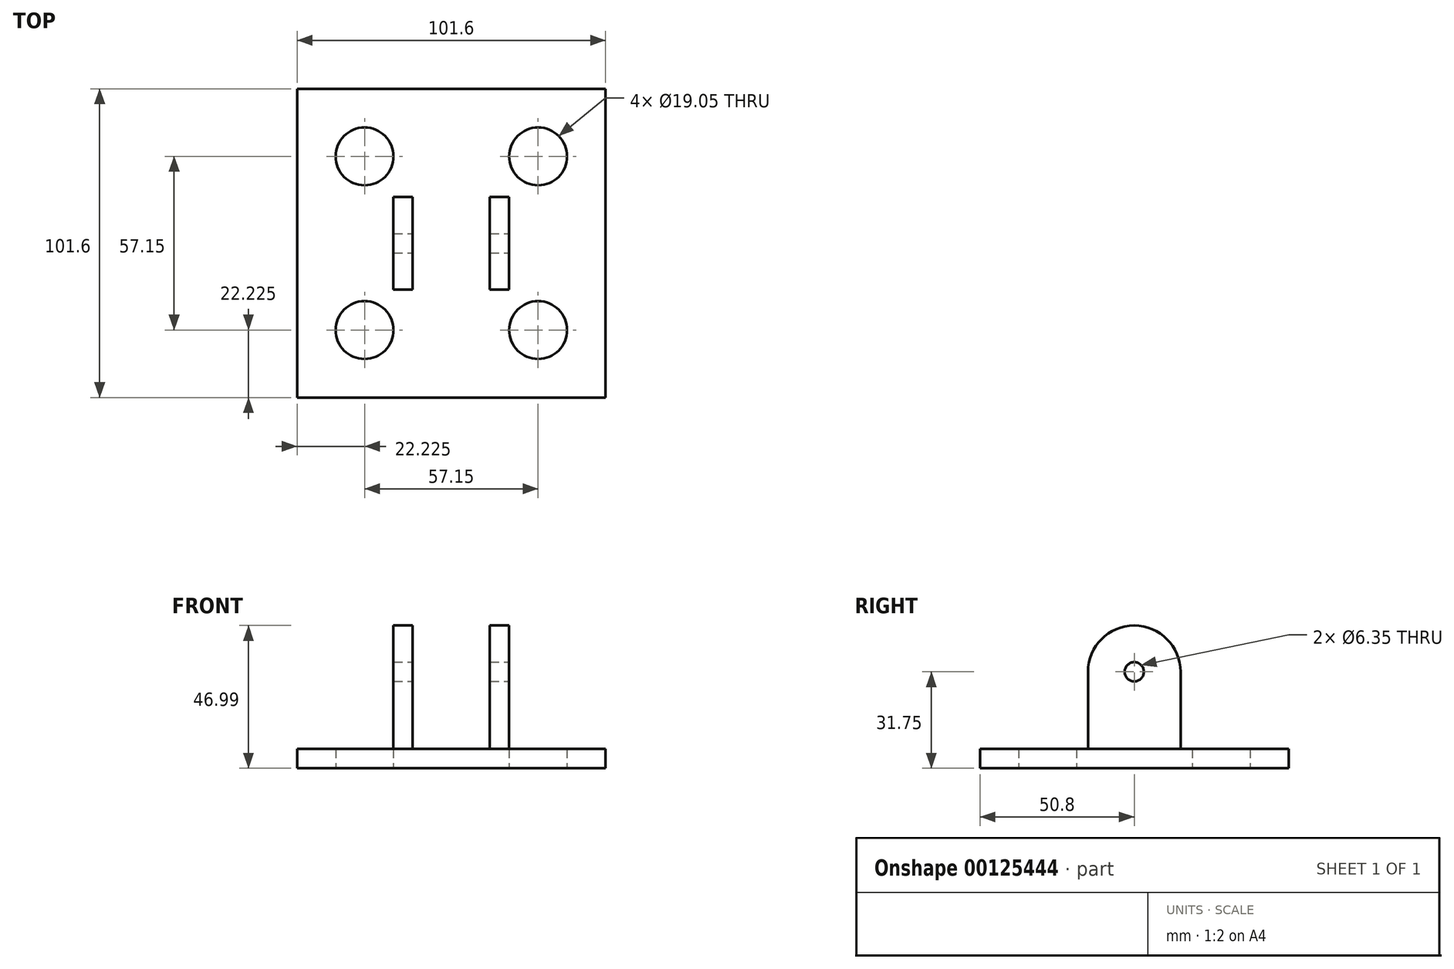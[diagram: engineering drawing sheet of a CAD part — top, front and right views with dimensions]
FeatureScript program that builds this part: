
annotation { "Feature Type Name" : "Feature", "Feature Type Description" : "" }
export const myFeature = defineFeature(function(context is Context, id is Id, definition is map)
    precondition{}
    {
        {
            var Q0;
            Q0=qCreatedBy(makeId("Top.planeOp"),FACE);
            var sketch = newSketch(context, id + "F0", { "sketchPlane" : qUnion([Q0])});
            skLineSegment(sketch, "E0.bottom", {"start": v(50.8, -50.8) * mm, "end": v(-50.8, -50.8) * mm});
            skLineSegment(sketch, "E0.top", {"start": v(50.8, 50.8) * mm, "end": v(-50.8, 50.8) * mm});
            skLineSegment(sketch, "E0.left", {"start": v(50.8, -50.8) * mm, "end": v(50.8, 50.8) * mm});
            skLineSegment(sketch, "E0.right", {"start": v(-50.8, -50.8) * mm, "end": v(-50.8, 50.8) * mm});
            skPoint(sketch, "E0.middle", {"position": v(0, 0) * mm});
            skCircle(sketch, "E1", {"center": v(-28.58, 28.58) * mm, "radius": 9.53 * mm});
            skCircle(sketch, "E2.MirrorC", {"center": v(28.58, 28.58) * mm, "radius": 9.53 * mm});
            skCircle(sketch, "E3.MirrorC", {"center": v(28.58, -28.58) * mm, "radius": 9.53 * mm});
            skCircle(sketch, "E4.MirrorC", {"center": v(-28.58, -28.58) * mm, "radius": 9.53 * mm});
            skSolve(sketch);
        }
        {
            var Q0;
            Q0=makeQuery(id+"F0.imprint","IMPRINT",FACE,{"disambiguationData":[TD([[makeQuery(id+"F0.imprint","IMPRINT",EDGE,{"derivedFrom":sQuery(id+"F0.wireOp",EDGE,"E0.bottom")}),-1.0]])]});
            extrude(context, id + "F1", {"entities" : qUnion([Q0]), "depth" : 6.35 * mm});
        }
        {
            var Q0;
            Q0=makeQuery(id+"F1.opExtrude","CAP_FACE",FACE,{"disambiguationData":[OSD([sQuery(id+"F0.wireOp",EDGE,"E0.bottom"),sQuery(id+"F0.wireOp",EDGE,"E0.top"),sQuery(id+"F0.wireOp",EDGE,"E0.left"),sQuery(id+"F0.wireOp",EDGE,"E0.right"),sQuery(id+"F0.wireOp",EDGE,"E1"),sQuery(id+"F0.wireOp",EDGE,"E2.MirrorC"),sQuery(id+"F0.wireOp",EDGE,"E3.MirrorC"),sQuery(id+"F0.wireOp",EDGE,"E4.MirrorC")])],"isStart":false});
            var sketch = newSketch(context, id + "F2", { "sketchPlane" : qUnion([Q0])});
            skLineSegment(sketch, "E5.bottom", {"start": v(12.7, -15.24) * mm, "end": v(-12.7, -15.24) * mm});
            skLineSegment(sketch, "E5.top", {"start": v(12.7, 15.24) * mm, "end": v(-12.7, 15.24) * mm});
            skLineSegment(sketch, "E5.left", {"start": v(12.7, -15.24) * mm, "end": v(12.7, 15.24) * mm});
            skLineSegment(sketch, "E5.right", {"start": v(-12.7, -15.24) * mm, "end": v(-12.7, 15.24) * mm});
            skPoint(sketch, "E5.middle", {"position": v(0, 0) * mm});
            skLineSegment(sketch, "E6.bottom", {"start": v(19.05, -15.24) * mm, "end": v(-19.05, -15.24) * mm});
            skLineSegment(sketch, "E6.top", {"start": v(19.05, 15.24) * mm, "end": v(-19.05, 15.24) * mm});
            skLineSegment(sketch, "E6.left", {"start": v(19.05, -15.24) * mm, "end": v(19.05, 15.24) * mm});
            skLineSegment(sketch, "E6.right", {"start": v(-19.05, -15.24) * mm, "end": v(-19.05, 15.24) * mm});
            skSolve(sketch);
        }
        {
            var Q0;
            {var subQ0=sQuery(id+"F2.wireOp",EDGE,"E5.left");Q0=makeQuery(id+"F2.imprint","IMPRINT",FACE,{"disambiguationData":[TD([[makeQuery(id+"F2.imprint","IMPRINT",EDGE,{"derivedFrom":subQ0}),-1.0]])]});}
            var Q1;
            {var subQ0=sQuery(id+"F2.wireOp",EDGE,"E5.right");Q1=makeQuery(id+"F2.imprint","IMPRINT",FACE,{"disambiguationData":[TD([[makeQuery(id+"F2.imprint","IMPRINT",EDGE,{"derivedFrom":subQ0}),1.0]])]});}
            extrude(context, id + "F3", {"entities" : qUnion([Q0, Q1]), "operationType" : NewBodyOperationType.ADD, "depth" : 25.4 * mm});
        }
        {
            var Q0;
            Q0=makeQuery(id+"F3.opExtrude","CAP_FACE",FACE,{"disambiguationData":[OSD([sQuery(id+"F2.wireOp",EDGE,"E5.left"),sQuery(id+"F2.wireOp",EDGE,"E6.bottom"),sQuery(id+"F2.wireOp",EDGE,"E6.top"),sQuery(id+"F2.wireOp",EDGE,"E6.left")])],"isStart":false});
            var sketch = newSketch(context, id + "F4", { "sketchPlane" : qUnion([Q0])});
            skLineSegment(sketch, "E7", {"start": v(12.7, 0) * mm, "end": v(19.05, 0) * mm});
            skSolve(sketch);
        }
        {
            var Q0;
            Q0 = qSketchRegion(id + "F4", true);
            var Q1;
            {var subQ0=sQuery(id+"F4.wireOp",EDGE,"E7");Q1=makeQuery(id+"F4.imprint","IMPRINT",FACE,{"disambiguationData":[TD([[makeQuery(id+"F4.imprint","IMPRINT",EDGE,{"derivedFrom":subQ0}),-1.0]])]});}
            var Q2;
            Q2=sQuery(id+"F4.wireOp",EDGE,"E7");
            revolve(context, id + "F5", {"operationType" : NewBodyOperationType.ADD, "entities" : qUnion([Q0, Q1]), "axis" : qUnion([Q2]), "revolveType" : RevolveType.FULL});
        }
        {
            var Q0;
            Q0=makeQuery(id+"F1.opExtrude","SWEPT_BODY",BODY,{"disambiguationData":[OSD([sQuery(id+"F0.wireOp",EDGE,"E0.bottom"),sQuery(id+"F0.wireOp",EDGE,"E0.top"),sQuery(id+"F0.wireOp",EDGE,"E0.left"),sQuery(id+"F0.wireOp",EDGE,"E0.right"),sQuery(id+"F0.wireOp",EDGE,"E1"),sQuery(id+"F0.wireOp",EDGE,"E2.MirrorC"),sQuery(id+"F0.wireOp",EDGE,"E3.MirrorC"),sQuery(id+"F0.wireOp",EDGE,"E4.MirrorC")])]});
            var Q1;
            Q1=qCreatedBy(makeId("Right.planeOp"),FACE);
            mirror(context, id + "F6", {"operationType" : NewBodyOperationType.ADD, "entities" : qUnion([Q0]), "mirrorPlane" : qUnion([Q1])});
        }
        {
            var Q0;
            {var subQ0=sQuery(id+"F2.wireOp",EDGE,"E6.left");Q0=makeQuery(id+"F5.boolean.opBoolean","MERGE",FACE,{"derivedFrom":[makeQuery(id+"F3.opExtrude","SWEPT_FACE",FACE,{"disambiguationData":[OSD([subQ0])]}),makeQuery(id+"F5.opRevolve","SWEPT_FACE",FACE,{"disambiguationData":[OSD([subQ0])]})]});}
            var sketch = newSketch(context, id + "F7", { "sketchPlane" : qUnion([Q0])});
            skCircle(sketch, "E8", {"center": v(0, 31.75) * mm, "radius": 3.18 * mm});
            skSolve(sketch);
        }
        {
            var Q0;
            Q0 = qSketchRegion(id + "F7", true);
            extrude(context, id + "F8", {"entities" : qUnion([Q0]), "operationType" : NewBodyOperationType.REMOVE, "oppositeDirection" : true, "depth" : 44.45 * mm});
        }
    });
